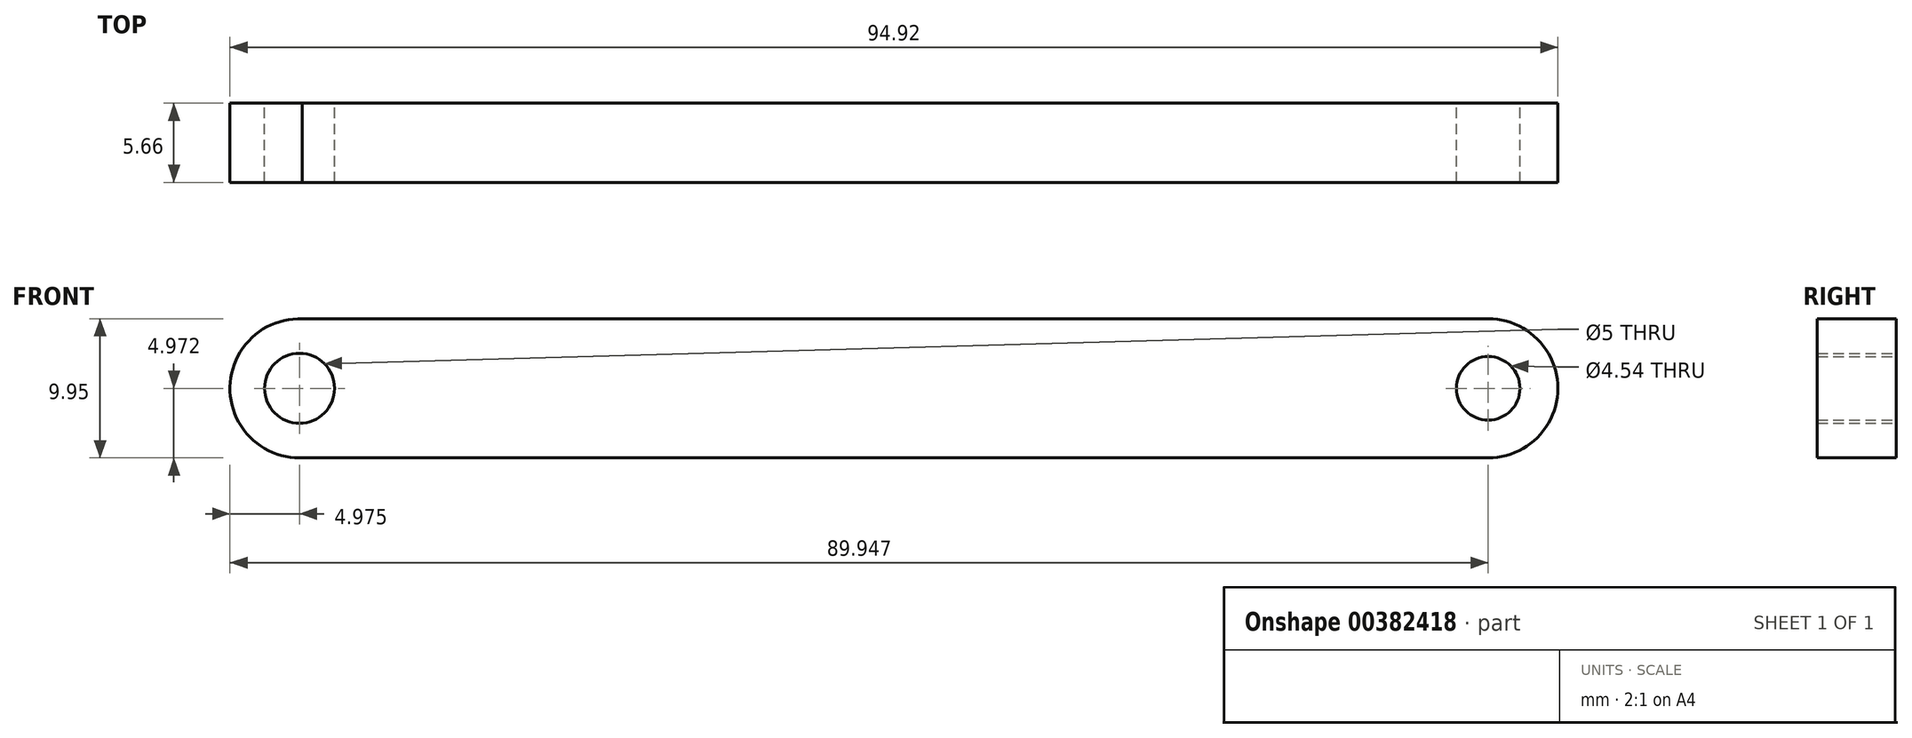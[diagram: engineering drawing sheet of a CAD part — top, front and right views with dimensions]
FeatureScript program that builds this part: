
annotation { "Feature Type Name" : "Feature", "Feature Type Description" : "" }
export const myFeature = defineFeature(function(context is Context, id is Id, definition is map)
    precondition{}
    {
        {
            var Q0;
            Q0=qCreatedBy(makeId("Front.planeOp"),FACE);
            var sketch = newSketch(context, id + "F0", { "sketchPlane" : qUnion([Q0])});
            skArc(sketch, "E0", {"start": v(-29.65, 18.23) * mm, "mid": v(-34.82, 13.36) * mm, "end": v(-29.85, 8.29) * mm});
            skArc(sketch, "E1", {"start": v(55.13, 8.29) * mm, "mid": v(60.1, 13.26) * mm, "end": v(55.13, 18.24) * mm});
            skLineSegment(sketch, "E2", {"start": v(-30.04, 18.23) * mm, "end": v(55.13, 18.24) * mm});
            skLineSegment(sketch, "E3", {"start": v(55.13, 8.29) * mm, "end": v(-29.85, 8.29) * mm});
            skCircle(sketch, "E4", {"center": v(-29.85, 13.26) * mm, "radius": 2.5 * mm});
            skCircle(sketch, "E5", {"center": v(55.13, 13.26) * mm, "radius": 2.27 * mm});
            skSolve(sketch);
        }
        {
            var Q0;
            Q0 = qSketchRegion(id + "F0", true);
            extrude(context, id + "F1", {"entities" : qUnion([Q0]), "depth" : 5.66 * mm});
        }
    });
